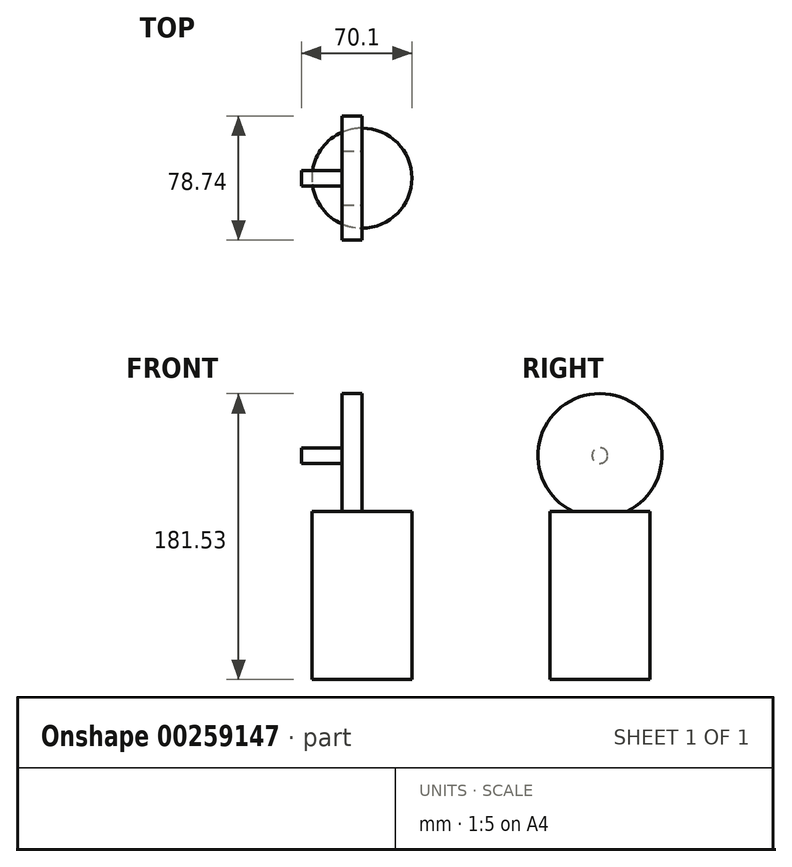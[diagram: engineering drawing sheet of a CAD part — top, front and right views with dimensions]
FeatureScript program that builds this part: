
annotation { "Feature Type Name" : "Feature", "Feature Type Description" : "" }
export const myFeature = defineFeature(function(context is Context, id is Id, definition is map)
    precondition{}
    {
        {
            var Q0;
            Q0=qCreatedBy(makeId("Top.planeOp"),FACE);
            var sketch = newSketch(context, id + "F0", { "sketchPlane" : qUnion([Q0])});
            skCircle(sketch, "E0", {"center": v(0, 0) * mm, "radius": 31.75 * mm});
            skSolve(sketch);
        }
        {
            var Q0;
            Q0 = qSketchRegion(id + "F0", true);
            extrude(context, id + "F1", {"entities" : qUnion([Q0]), "depth" : 106.68 * mm});
        }
        {
            var Q0;
            Q0=makeQuery(id+"F1.opExtrude","CAP_FACE",FACE,{"disambiguationData":[OSD([sQuery(id+"F0.wireOp",EDGE,"E0")])],"isStart":false});
            var sketch = newSketch(context, id + "F2", { "sketchPlane" : qUnion([Q0])});
            skLineSegment(sketch, "E1", {"start": v(0, 76.84) * mm, "end": v(0, -77.7) * mm});
            skSolve(sketch);
        }
        {
            var Q0;
            Q0=sQuery(id+"F2.wireOp",EDGE,"E1");
            cPlane(context, id + "F3", {"entities" : qUnion([Q0]), "cplaneType" : CPlaneType.LINE_ANGLE, "offset" : 25.4 * mm, "angle" : 90 * degree, "oppositeDirection" : true, "width" : 152.4 * mm, "height" : 152.4 * mm});
        }
        {
            var Q0;
            Q0=qCreatedBy(id+"F3.planeOp",FACE);
            var sketch = newSketch(context, id + "F4", { "sketchPlane" : qUnion([Q0])});
            skCircle(sketch, "E2", {"center": v(0, 142.16) * mm, "radius": 39.37 * mm});
            skSolve(sketch);
        }
        {
            var Q0;
            Q0 = qSketchRegion(id + "F4", true);
            extrude(context, id + "F5", {"entities" : qUnion([Q0]), "operationType" : NewBodyOperationType.ADD, "depth" : 12.7 * mm});
        }
        {
            var Q0;
            Q0=makeQuery(id+"F5.opExtrude","CAP_FACE",FACE,{"disambiguationData":[OSD([sQuery(id+"F4.wireOp",EDGE,"E2")])],"isStart":false});
            var sketch = newSketch(context, id + "F6", { "sketchPlane" : qUnion([Q0])});
            skCircle(sketch, "E3", {"center": v(0, 142.16) * mm, "radius": 4.95 * mm});
            skSolve(sketch);
        }
        {
            var Q0;
            Q0 = qSketchRegion(id + "F6", true);
            extrude(context, id + "F7", {"entities" : qUnion([Q0]), "operationType" : NewBodyOperationType.ADD, "depth" : 25.65 * mm});
        }
    });
